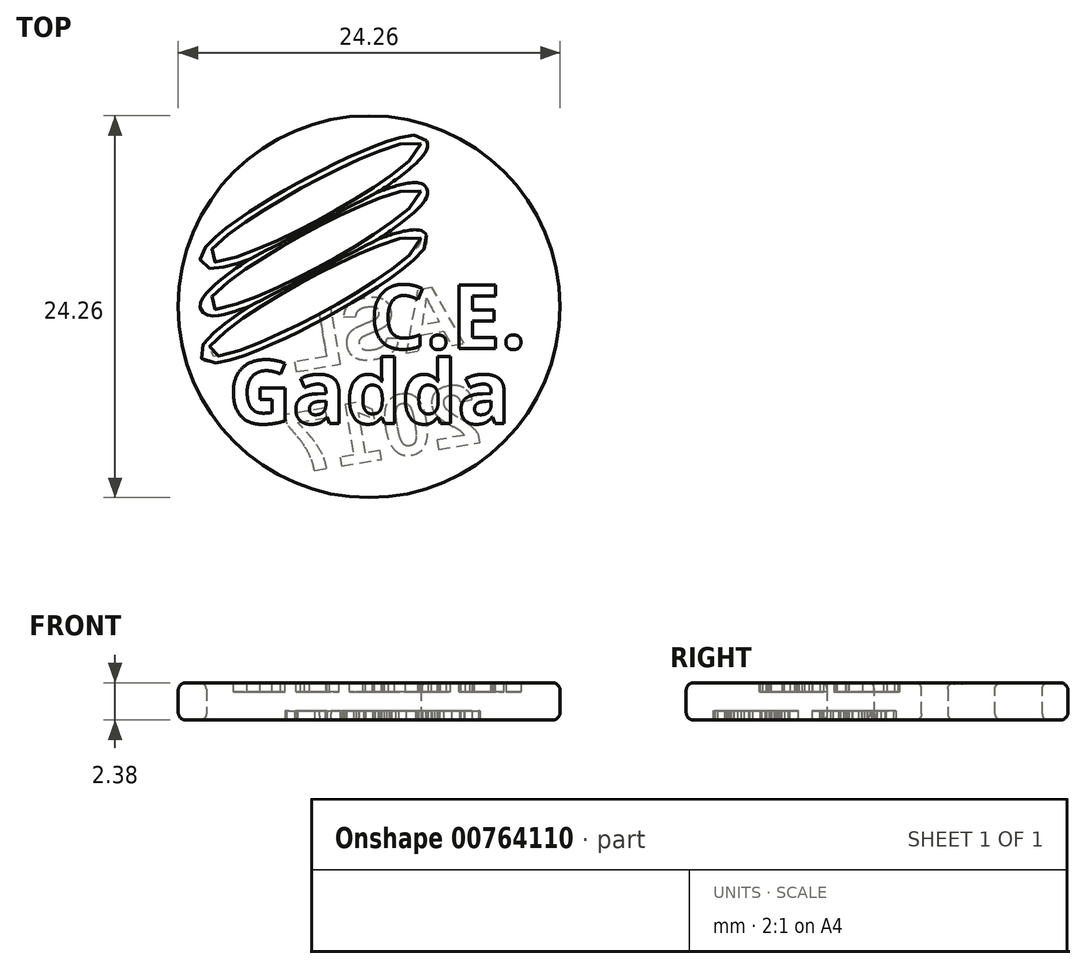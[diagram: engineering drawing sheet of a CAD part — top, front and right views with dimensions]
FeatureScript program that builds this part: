
annotation { "Feature Type Name" : "Feature", "Feature Type Description" : "" }
export const myFeature = defineFeature(function(context is Context, id is Id, definition is map)
    precondition{}
    {
        {
            assignVariable(context, id + "F0", {"name" : "SPES", "anyValue" : 2.38});
        }
        {
            var Q0;
            Q0=qCreatedBy(makeId("Top.planeOp"),FACE);
            var sketch = newSketch(context, id + "F1", { "sketchPlane" : qUnion([Q0])});
            skCircle(sketch, "E0", {"center": v(0, 0) * mm, "radius": 12.12 * mm});
            skEllipse(sketch, "E1", {"center": v(-3.52, 6.66) * mm, "majorRadius": 7.74 * mm, "minorRadius": 1.14 * mm, "majorAxis": v(0.88, 0.48)});
            skEllipse(sketch, "E2.1.0.0", {"center": v(-3.52, 3.66) * mm, "majorRadius": 7.74 * mm, "minorRadius": 1.14 * mm, "majorAxis": v(0.88, 0.48)});
            skEllipse(sketch, "E2.2.0.0", {"center": v(-3.52, 0.66) * mm, "majorRadius": 7.74 * mm, "minorRadius": 1.14 * mm, "majorAxis": v(0.88, 0.48)});
            skLineSegment(sketch, "E2.direction1", {"start": v(-3.52, 6.66) * mm, "end": v(-3.52, 3.66) * mm, "construction": true});
            skSolve(sketch);
        }
        {
            var Q0;
            Q0=makeQuery(id+"F1.imprint","IMPRINT",FACE,{"disambiguationData":[TD([[makeQuery(id+"F1.imprint","IMPRINT",EDGE,{"derivedFrom":sQuery(id+"F1.wireOp",EDGE,"E0")}),1.0]])]});
            extrude(context, id + "F2", {"entities" : qUnion([Q0]), "depth" : (getVariable(context, 'SPES')) * mm, "offsetDistance" : 25 * mm});
        }
        {
            var Q0;
            Q0=makeQuery(id+"F2.opExtrude","CAP_EDGE",EDGE,{"disambiguationData":[OSD([sQuery(id+"F1.wireOp",EDGE,"E0")])],"isStart":true});
            var Q1;
            Q1=makeQuery(id+"F2.opExtrude","CAP_EDGE",EDGE,{"disambiguationData":[OSD([sQuery(id+"F1.wireOp",EDGE,"E0")])],"isStart":false});
            fillet(context, id + "F3", {"entities" : qUnion([Q0, Q1]), "radius" : .5 * mm, "tangentPropagation" : true, "allowEdgeOverflow" : false});
        }
        {
            var Q0;
            Q0=makeQuery(id+"F2.opExtrude","CAP_FACE",FACE,{"disambiguationData":[OSD([sQuery(id+"F1.wireOp",EDGE,"E0"),sQuery(id+"F1.wireOp",EDGE,"E1"),sQuery(id+"F1.wireOp",EDGE,"E2.1.0.0"),sQuery(id+"F1.wireOp",EDGE,"E2.2.0.0")])],"isStart":false});
            var sketch = newSketch(context, id + "F4", { "sketchPlane" : qUnion([Q0])});
            skText(sketch, "E3", { "text": "C.E.", "fontName": "OpenSans-Bold.ttf"});
            skText(sketch, "E4", { "text": "Gadda", "fontName": "NotoSans-Bold.ttf"});
            const initialGuessF4  = {"E3": [0, -0.00266, 1, 0.00077, 0.00406], "E4": [-0.00895, -0.00742, 1, 0, 0.00404]};
            skSetInitialGuess(sketch, initialGuessF4);
            skSolve(sketch);
        }
        {
            var Q0;
            Q0 = qSketchRegion(id + "F4", true);
            extrude(context, id + "F5", {"entities" : qUnion([Q0]), "operationType" : NewBodyOperationType.REMOVE, "oppositeDirection" : true, "depth" : .6 * mm, "offsetDistance" : 25 * mm});
        }
        {
            var Q0;
            Q0=makeQuery(id+"F2.opExtrude","CAP_EDGE",EDGE,{"disambiguationData":[OSD([sQuery(id+"F1.wireOp",EDGE,"E2.1.0.0")])],"isStart":false});
            var Q1;
            Q1=makeQuery(id+"F2.opExtrude","CAP_EDGE",EDGE,{"disambiguationData":[OSD([sQuery(id+"F1.wireOp",EDGE,"E2.2.0.0")])],"isStart":false});
            var Q2;
            Q2=makeQuery(id+"F2.opExtrude","CAP_EDGE",EDGE,{"disambiguationData":[OSD([sQuery(id+"F1.wireOp",EDGE,"E1")])],"isStart":false});
            var Q3;
            Q3=makeQuery(id+"F2.opExtrude","CAP_EDGE",EDGE,{"disambiguationData":[OSD([sQuery(id+"F1.wireOp",EDGE,"E1")])],"isStart":true});
            var Q4;
            Q4=makeQuery(id+"F2.opExtrude","CAP_EDGE",EDGE,{"disambiguationData":[OSD([sQuery(id+"F1.wireOp",EDGE,"E2.1.0.0")])],"isStart":true});
            var Q5;
            Q5=makeQuery(id+"F2.opExtrude","CAP_EDGE",EDGE,{"disambiguationData":[OSD([sQuery(id+"F1.wireOp",EDGE,"E2.2.0.0")])],"isStart":true});
            fillet(context, id + "F6", {"entities" : qUnion([Q0, Q1, Q2, Q3, Q4, Q5]), "radius" : .4 * mm, "tangentPropagation" : true, "allowEdgeOverflow" : false});
        }
        {
            var Q0;
            Q0=makeQuery(id+"F2.opExtrude","CAP_FACE",FACE,{"disambiguationData":[OSD([sQuery(id+"F1.wireOp",EDGE,"E0"),sQuery(id+"F1.wireOp",EDGE,"E1"),sQuery(id+"F1.wireOp",EDGE,"E2.1.0.0"),sQuery(id+"F1.wireOp",EDGE,"E2.2.0.0")])],"isStart":true});
            var sketch = newSketch(context, id + "F7", { "sketchPlane" : qUnion([Q0])});
            skText(sketch, "E5", { "text": "ASL\n2017", "fontName": "Arimo-Bold.ttf"});
            skPoint(sketch, "E6", {"position": v(-4.08, -8.26) * mm});
            const initialGuessF7  = {"E5": [0.00616, 0.0023, -0.9859, 0.16728, 0.004]};
            skSetInitialGuess(sketch, initialGuessF7);
            skSolve(sketch);
        }
        {
            var Q0;
            Q0 = qSketchRegion(id + "F7", true);
            extrude(context, id + "F8", {"entities" : qUnion([Q0]), "operationType" : NewBodyOperationType.REMOVE, "oppositeDirection" : true, "depth" : .6 * mm, "offsetDistance" : 25 * mm});
        }
    });
